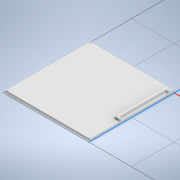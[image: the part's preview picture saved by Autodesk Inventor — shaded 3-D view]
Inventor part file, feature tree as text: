
AUTODESK INVENTOR PART (.ipt)
format: ipt  version: 2020 (Build 240168000, 168)  size: 308,224 bytes
history: native  units: in
note: dims shown in document units (in); Inventor stores cm internally (conversion verified against a paired STEP export)
features: extrude x11, sketch x6, fillet x5, hole x2, plane x2, shell x1, split x1
ambient origin geometry x8: Origin, YZ Plane, XZ Plane, XY Plane, X Axis, Y Axis, Z Axis, Center Point
bodies: Solid1 (feature_tree)
feature tree (28):
  extrude  "Extrusion1"  Depth=7.874in
  shell  "Shell1"  Thickness=7.874in
  extrude  "Extrusion2"  Depth=0.3937in
  fillet  "Fillet1"  Radius=0.3937in
  sketch  "Sketch3"  dims[d7=6.1024in d8=1.6339in d9=0.3937in d10=0.0in]
  extrude  "Extrusion3"  Depth=0.0787in
  hole  "Hole1"  [1 undecoded]
  fillet  "Fillet2"  Radius=0.8661in
  extrude  "Extrusion4"  Depth=1.1417in
  sketch  "Sketch4"  dims[d11=0.0787in d12=1.5748in]
  extrude  "Extrusion5"  Depth=0.3937in
  extrude  "Extrusion6"  Depth=0.0787in TaperAngle=0.0deg
  extrude  "Extrusion7"  Depth=0.0394in
  extrude  "Extrusion8"  Depth=0.0394in
  fillet  "Fillet3"  Radius=0.1575in
  fillet  "Fillet4"  Radius=0.1575in
  extrude  "Extrusion9"  Depth=0.1969in
  plane  "Work Plane1"
  extrude  "Extrusion10"  Depth=0.1969in
  plane  "Work Plane4"
  split  "Split1"
  extrude  "Extrusion11"  Depth=0.3937in
  hole  "Hole2"  [1 undecoded]
  fillet  "Fillet5"  Radius=0.3937in
  sketch  "Sketch1"  dims[d0=7.874in d1=7.874in d2=7.874in d3=0.0in]
  sketch  "Sketch5"  dims[d13=1.5748in d16=3.1496in d19=0.8661in]
  sketch  "Sketch6"  dims[d20=0.1575in d22=1.1417in]
  sketch  "Sketch7"  dims[d23=0.3937in d24=0.3937in d25=0.0787in d26=0.0in d27=2.8346in d28=0.9843in d29=0.1575in d30=0.1575in d31=0.1969in d32=0.1969in d33=0.3937in d34=0.3937in d35=0.3937in d36=0.1378in d37=0.2362in d38=0.1575in d39=0.0787in d40=90.0deg d41=0.315in d42=0.8108in d43=0.1181in d44=3.937in d45=0.1969in d46=0.0in d47=0.0787in d48=0.0591in d49=3.1496in d50=0.0in d51=2.3622in d52=0.0in d53=1.5748in d54=0.0in d55=0.7874in d56=0.0in d57=0.1181in d58=0.1575in d59=1.5748in d60=0.0in d61=-0.5906in d62=0.9843in d63=0.0in d65=0.0in d66=0.3937in d67=0.1969in d68=0.1969in d69=0.2362in d70=0.0in d71=0.1969in d72=4.3307in d73=0.1969in d74=0.0984in d75=0.0984in d76=0.0984in d77=0.0984in d78=0.0984in d79=0.0984in d80=0.0984in d81=0.0984in d82=0.0787in d83=0.2362in d84=0.1575in d85=0.1181in d86=90.0deg d87=0.5906in d88=0.0in d89=0.1969in d90=0.2362in d5=0.0394in d6=0.0394in d14=0.0025in d15=0.0295in d64=0.0197in d91=0.0394in d92=0.0394in d93=0.0059in d94=0.0098in d95=0.0148in d96=0.5635in d97=0.0295in d98=0.8108in d99=0.0025in d100=0.0295in d101=0.0148in]
note: 2 required parameter values undecoded (feature->parameter linkage not recoverable at this tier; creation-order binding heuristic only, values carry confidence <= 0.55)
